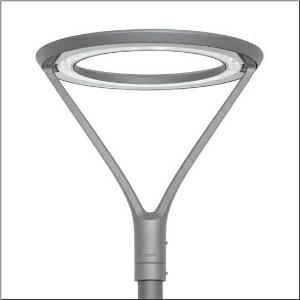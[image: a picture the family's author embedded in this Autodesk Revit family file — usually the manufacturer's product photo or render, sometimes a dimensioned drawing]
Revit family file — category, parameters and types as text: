
# Revit family: dl_20___pl1_2s_5xa512832s008_4b44
name_source: partatom
category: Lighting Fixtures
units: mm (PartAtom-declared; Revit-internal decimal feet)

## family parameters
Cut with Voids When Loaded = No
Host = Face
Light Source = No
Part Type = Normal
Room Calculation Point = No
Round Connector Dimension = Use Diameter
Shared = No

## types (1)
- --- (1 x LED, 3050 lm, 30.4 W, 2200K)
    Apparent Load = 30 VA
    CIE Flux Codes = 33 78 99 100 100
    Color Rendering = 70
    Color Temperature = 2200K
    Default Elevation = 1800 mm
    Description = DL® 20, mast luminaire, primary light control with reflector, highly specular, primary optical cover: cover, of toughened safety glass of clear glass with excellent transmission level, light distribution: PL1.2s, light emission: direct distribution, primary light characteristic: symmetric, installation type: post-top, LED, High Power LED, rated luminous flux: 3.040lm, luminous efficacy: 86lm/W, light colour: 722, colour temperature: 2200K, control gear: Plus, control: flexible luminous flux parameterisation, time-dependent luminous flux control, constant luminous flux control, digital communication interface, power reduction, overheat protection, electronic power reduction, mains connection: 230..240V, 50/60Hz, connection cable pre-assembled, cable length: 5m, start of lifetime: 36W, end of service life: 36W, reduction: 17W, luminaire housing, upper part, of cast aluminium, powder-coated, Siteco® metallic grey (DB 702S), diameter: 690mm, height: 690mm, spigot size: 76mm (post-top), mounting height: 4..6m, luminaire housing, of cast aluminium, powder-coated, Siteco® metallic grey (DB 702S), equipment: standard, protection rating (complete): IP66, insulation class (complete): insulation class II (safety insulation), certification: CE, ENEC, VDE, impact resistance: IK08, permissible operating ambient temperature: -25..+35°C, standard-compliant lighting for roads and squares, packaging unit: 1 piece

Light Distribution: PL1.2s
    Height = 690 mm
    Lamp = 1 x LED
    Lamp Light Flux = 3050 lm
    Lamp Power = 30.4 W
    Lamp count = 1
    Length = 690 mm
    Luminous efficacy = 100 lm/W
    Manufacturer = Siteco
    ModVariant = No
    Model = 5XA512832S008
    Number of Poles = 1
    OnlyDefault = Yes
    Power Factor = 1
    Product Name = DL 20 | PL1.2s
    Product group = mast luminaire | pylon top
    ProductGroupID = 6100
    Protection Class = Protection class II
    Protection Degree = IP 66
    RLX_Detail_Level = 1
    RLX_Emergency_Light_Flux = 0 lm
    RLX_Emergency_Type = 0
    RLX_Emergency_Type_DB = No
    RlxData = <blob elided: 204365 chars, md5=b38f22d9>
    Socket = socket
    Standby Power = 0 W
    System Light Flux = 3050 lm
    System Power = 30 W
    Type Comments = factory setting: luminous flux: 100 % | dim-lin: 254 | 412 mA
    Type Image = l_1006001.jpg
    URL = http://relux.com
    VarID = @adj_084747
    Voltage = 0 V
    Weight = 0.00 kg
    Width = 0 mm  [stored 0 ft]

note: [stored X ft] marks values corroborated as IEEE doubles in the binary element streams (Revit-internal decimal feet)

## geometry (parser evidence)
native form markers: Blend x4, Sweep x8
no freeform markers — native parametric forms only
